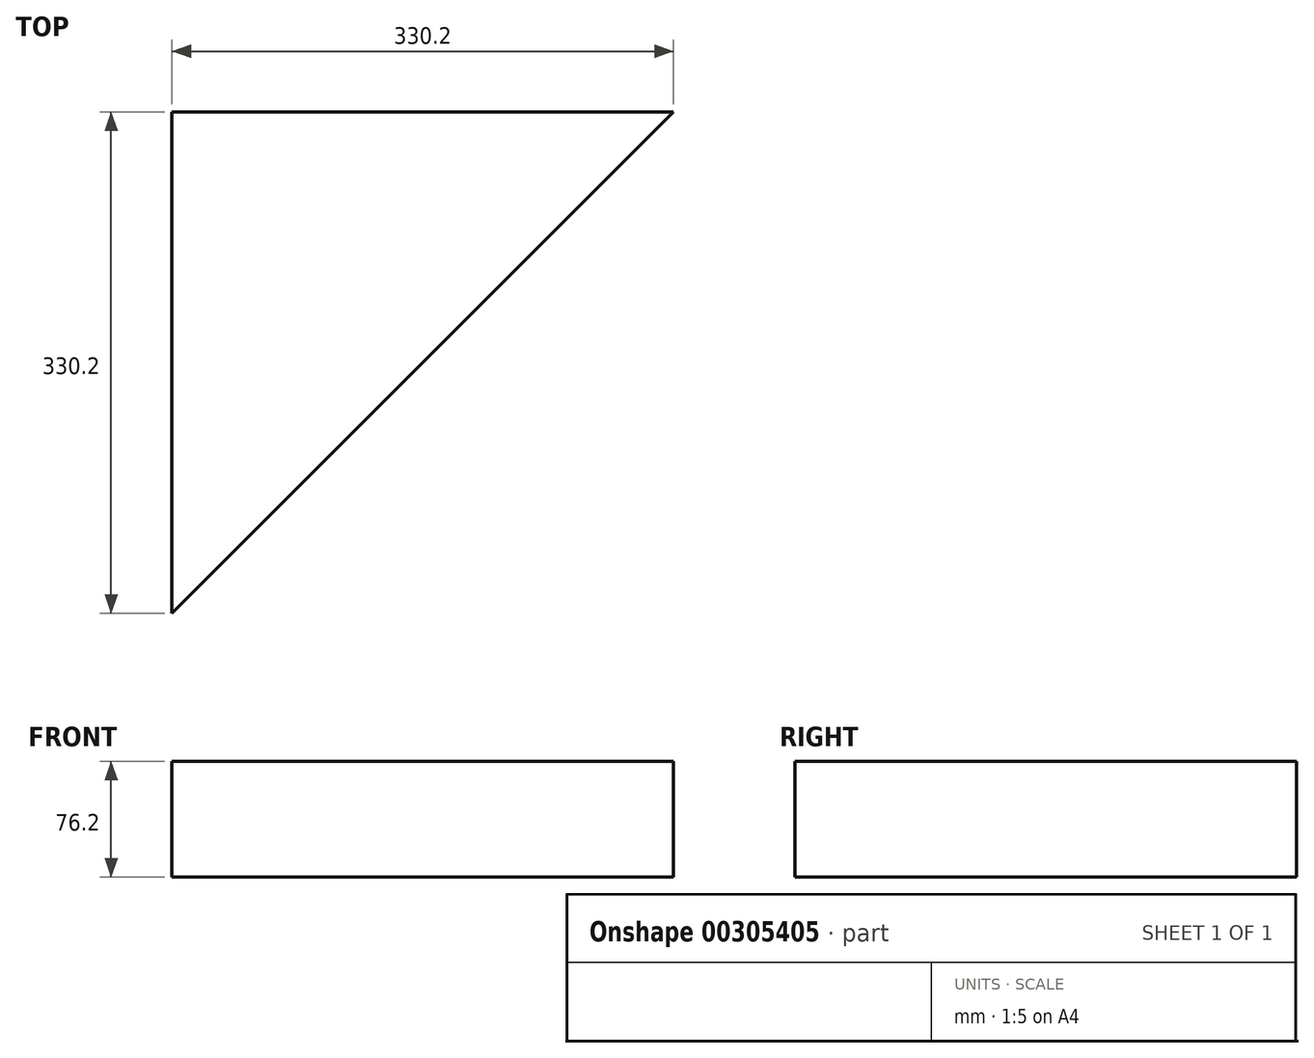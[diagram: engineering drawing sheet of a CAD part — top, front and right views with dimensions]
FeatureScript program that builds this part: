
annotation { "Feature Type Name" : "Feature", "Feature Type Description" : "" }
export const myFeature = defineFeature(function(context is Context, id is Id, definition is map)
    precondition{}
    {
        {
            var Q0;
            Q0=qCreatedBy(makeId("Top.planeOp"),FACE);
            var sketch = newSketch(context, id + "F0", { "sketchPlane" : qUnion([Q0])});
            skLineSegment(sketch, "E0.bottom", {"start": v(-153.25, 180.93) * mm, "end": v(176.95, 180.93) * mm});
            skLineSegment(sketch, "E0.left", {"start": v(-153.25, 180.93) * mm, "end": v(-153.25, -149.27) * mm});
            skLineSegment(sketch, "E1", {"start": v(-153.25, -149.27) * mm, "end": v(176.95, 180.93) * mm});
            skSolve(sketch);
        }
        {
            var Q0;
            Q0=makeQuery(id+"F0.imprint","IMPRINT",FACE,{"disambiguationData":[TD([[makeQuery(id+"F0.imprint","IMPRINT",EDGE,{"derivedFrom":sQuery(id+"F0.wireOp",EDGE,"E0.bottom")}),-1.0]])]});
            extrude(context, id + "F1", {"entities" : qUnion([Q0]), "depth" : 76.2 * mm});
        }
    });
